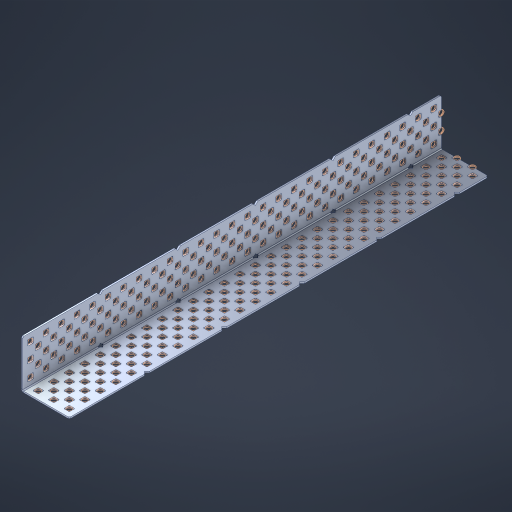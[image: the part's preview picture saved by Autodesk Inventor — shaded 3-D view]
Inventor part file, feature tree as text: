
AUTODESK INVENTOR PART (.ipt)
format: ipt  version: 2023 (Build 270158000, 158)  size: 2,800,128 bytes
history: native  units: in
note: dims shown in document units (in); Inventor stores cm internally (conversion verified against a paired STEP export)
features: extrude x62
bodies: Body1 (feature_tree), Body2 (feature_tree), Body3 (feature_tree), Body4 (feature_tree), Body5 (feature_tree), Body6 (feature_tree), Body7 (feature_tree), Body8 (feature_tree), Body9 (feature_tree), Body10 (feature_tree), Body11 (feature_tree), Body12 (feature_tree), Body13 (feature_tree), Body14 (feature_tree), Body15 (feature_tree), Body16 (feature_tree), Body17 (feature_tree), Body18 (feature_tree), Body19 (feature_tree), Body20 (feature_tree), Body21 (feature_tree), Body22 (feature_tree), Body23 (feature_tree), Body24 (feature_tree), Body25 (feature_tree), Body26 (feature_tree), Body27 (feature_tree), Body28 (feature_tree), Body29 (feature_tree), Body30 (feature_tree), Body31 (feature_tree), Body32 (feature_tree), Body33 (feature_tree), Body34 (feature_tree), Body35 (feature_tree), Body36 (feature_tree), Body37 (feature_tree), Body38 (feature_tree), Body39 (feature_tree), Body40 (feature_tree), Body41 (feature_tree), Body42 (feature_tree), Body43 (feature_tree), Body44 (feature_tree), Body45 (feature_tree), Body46 (feature_tree), Body47 (feature_tree), Body48 (feature_tree), Body49 (feature_tree), Body50 (feature_tree), Body51 (feature_tree), Body52 (feature_tree), Body53 (feature_tree), Body54 (feature_tree), Body55 (feature_tree), Body56 (feature_tree), Body57 (feature_tree), Body58 (feature_tree), Body59 (feature_tree), Body60 (feature_tree), Body61 (feature_tree), Body62 (feature_tree), Body63 (feature_tree), Body64 (feature_tree), Body65 (feature_tree), Body66 (feature_tree), Body67 (feature_tree), Body68 (feature_tree), Body69 (feature_tree), Body70 (feature_tree), Body71 (feature_tree), Body72 (feature_tree), Body73 (feature_tree), Body74 (feature_tree), Body75 (feature_tree), Body76 (feature_tree), Body77 (feature_tree), Body78 (feature_tree), Body79 (feature_tree), Body80 (feature_tree), Body81 (feature_tree), Body82 (feature_tree), Body83 (feature_tree), Body84 (feature_tree), Body85 (feature_tree), Body86 (feature_tree), Body87 (feature_tree), Body88 (feature_tree), Body89 (feature_tree), Body90 (feature_tree), Body91 (feature_tree), Body92 (feature_tree), Body93 (feature_tree), Body94 (feature_tree), Body95 (feature_tree), Body96 (feature_tree), Body97 (feature_tree), Body98 (feature_tree), Body99 (feature_tree), Body100 (feature_tree), Body101 (feature_tree), Body102 (feature_tree), Body103 (feature_tree), Body104 (feature_tree), Body105 (feature_tree), Body106 (feature_tree), Body107 (feature_tree), Body108 (feature_tree), Body109 (feature_tree), Body110 (feature_tree), Body111 (feature_tree), Body112 (feature_tree), Body113 (feature_tree), Body114 (feature_tree), Body115 (feature_tree), Body116 (feature_tree), Body117 (feature_tree), Body118 (feature_tree), Body119 (feature_tree), Body120 (feature_tree), Body121 (feature_tree), Body122 (feature_tree), Body123 (feature_tree), Body124 (feature_tree), Body125 (feature_tree), Body126 (feature_tree), Body127 (feature_tree), Body128 (feature_tree), Body129 (feature_tree), Body130 (feature_tree), Body131 (feature_tree), Body132 (feature_tree), Body133 (feature_tree), Body134 (feature_tree), Body135 (feature_tree), Body136 (feature_tree), Body137 (feature_tree), Body138 (feature_tree), Body139 (feature_tree), Body140 (feature_tree), Body141 (feature_tree), Body142 (feature_tree), Body143 (feature_tree), Body144 (feature_tree), Body145 (feature_tree), Body146 (feature_tree), Body147 (feature_tree), Body148 (feature_tree), Body149 (feature_tree), Body150 (feature_tree), Body151 (feature_tree), Body152 (feature_tree), Body153 (feature_tree), Body154 (feature_tree), Body155 (feature_tree), Body156 (feature_tree), Body157 (feature_tree), Body158 (feature_tree), Body159 (feature_tree), Body160 (feature_tree), Body161 (feature_tree), Body162 (feature_tree), Body163 (feature_tree), Body164 (feature_tree), Body165 (feature_tree), Body166 (feature_tree), Body167 (feature_tree), Body168 (feature_tree), Body169 (feature_tree), Body170 (feature_tree), Body171 (feature_tree), Body172 (feature_tree), Body173 (feature_tree), Body174 (feature_tree), Body175 (feature_tree), Body176 (feature_tree), Body177 (feature_tree), Body178 (feature_tree), Body179 (feature_tree), Body180 (feature_tree), Body181 (feature_tree), Body182 (feature_tree), Body183 (feature_tree), Body184 (feature_tree), Body185 (feature_tree), Body186 (feature_tree), Body187 (feature_tree), Body188 (feature_tree), Body189 (feature_tree), Body190 (feature_tree), Body191 (feature_tree), Body192 (feature_tree), Body193 (feature_tree), Body194 (feature_tree), Body195 (feature_tree), Body196 (feature_tree), Body197 (feature_tree), Body198 (feature_tree), Body199 (feature_tree), Body200 (feature_tree), Body201 (feature_tree), Body202 (feature_tree), Body203 (feature_tree), Body204 (feature_tree), Body205 (feature_tree), Body206 (feature_tree), Body207 (feature_tree), Body208 (feature_tree), Body209 (feature_tree), Body210 (feature_tree), Body211 (feature_tree), Body212 (feature_tree), Body213 (feature_tree), Body214 (feature_tree), Body215 (feature_tree), Body216 (feature_tree), Body217 (feature_tree), Body218 (feature_tree), Body219 (feature_tree), Body220 (feature_tree), Body221 (feature_tree), Body222 (feature_tree), Body223 (feature_tree), Body224 (feature_tree), Body225 (feature_tree), Body226 (feature_tree), Body227 (feature_tree), Body228 (feature_tree), Body229 (feature_tree), Body230 (feature_tree), Body231 (feature_tree), Body232 (feature_tree), Body233 (feature_tree), Body234 (feature_tree), Body235 (feature_tree), Body236 (feature_tree), Body237 (feature_tree), Body238 (feature_tree), Body239 (feature_tree), Body240 (feature_tree), Body241 (feature_tree), Body242 (feature_tree), Body243 (feature_tree), Body244 (feature_tree), Body245 (feature_tree), Body246 (feature_tree), Body247 (feature_tree), Body248 (feature_tree), Body249 (feature_tree), Body250 (feature_tree), Body251 (feature_tree), Body252 (feature_tree), Body253 (feature_tree), Body254 (feature_tree), Body255 (feature_tree), Body256 (feature_tree), Body257 (feature_tree), Body258 (feature_tree), Body259 (feature_tree), Body260 (feature_tree), Body261 (feature_tree), Body262 (feature_tree), Body263 (feature_tree), Body264 (feature_tree), Body265 (feature_tree), Body266 (feature_tree), Body267 (feature_tree), Body268 (feature_tree), Body269 (feature_tree), Body270 (feature_tree), Body271 (feature_tree)
feature tree (62):
  extrude  "ExtrusionSrf2195"  Depth=1.5in
  extrude  "ExtrusionSrf2196"  Depth=13.5in
  extrude  "ExtrusionSrf2197"  Depth=0.0469in
  extrude  "ExtrusionSrf2198"  Depth=0.0469in
  extrude  "ExtrusionSrf2199"  Depth=0.0234in
  extrude  "ExtrusionSrf2200"  Depth=0.0938in
  extrude  "ExtrusionSrf2201"  Depth=0.0469in
  extrude  "ExtrusionSrf2202"  Depth=1.5in TaperAngle=90.0deg
  extrude  "ExtrusionSrf2203"  Depth=0.1875in
  extrude  "ExtrusionSrf2204"  Depth=0.0469in
  extrude  "ExtrusionSrf2205"  Depth=0.0469in
  extrude  "ExtrusionSrf2206"  Depth=0.182in
  extrude  "ExtrusionSrf2207"  Depth=0.02in
  extrude  "ExtrusionSrf2208"  Depth=0.25in
  extrude  "ExtrusionSrf2209"  Depth=0.0469in
  extrude  "ExtrusionSrf2210"  TaperAngle=0.0deg  [1 undecoded]
  extrude  "ExtrusionSrf2211"  Depth=0.172in
  extrude  "ExtrusionSrf2212"  Depth=1.0in TaperAngle=0.0deg
  extrude  "ExtrusionSrf2213"  Depth=0.1473in
  extrude  "ExtrusionSrf2214"  Depth=0.1659in
  extrude  "ExtrusionSrf2215"  Depth=0.0469in
  extrude  "ExtrusionSrf2216"  Depth=0.04in TaperAngle=0.0deg
  extrude  "ExtrusionSrf2217"  Depth=2.5in
  extrude  "ExtrusionSrf2218"  Depth=0.25in TaperAngle=45.0deg
  extrude  "ExtrusionSrf2219"  Depth=0.182in
  extrude  "ExtrusionSrf2220"  Depth=0.02in
  extrude  "ExtrusionSrf2221"  Depth=0.0469in
  extrude  "ExtrusionSrf2222"  TaperAngle=0.0deg  [1 undecoded]
  extrude  "ExtrusionSrf2223"  Depth=0.172in
  extrude  "ExtrusionSrf2224"  Depth=0.5in TaperAngle=0.0deg
  extrude  "ExtrusionSrf2225"  Depth=0.5in
  extrude  "ExtrusionSrf2226"  Depth=0.0491in
  extrude  "ExtrusionSrf2227"  Depth=0.1227in
  extrude  "ExtrusionSrf2228"  Depth=0.08in
  extrude  "ExtrusionSrf2229"  Depth=0.04in
  extrude  "ExtrusionSrf2230"  Depth=2.5in
  extrude  "ExtrusionSrf2231"  Depth=0.25in
  extrude  "ExtrusionSrf2232"  Depth=10.6299in
  extrude  "ExtrusionSrf2233"  Depth=0.5in
  extrude  "ExtrusionSrf2234"  Depth=0.5in
  extrude  "ExtrusionSrf2235"  Depth=1.0in
  extrude  "ExtrusionSrf2236"  Depth=0.3937in
  extrude  "ExtrusionSrf2237"  Depth=0.071in
  extrude  "ExtrusionSrf2238"  Depth=0.5in
  extrude  "ExtrusionSrf2239"  [1 undecoded]
  extrude  "ExtrusionSrf2240"  [1 undecoded]
  extrude  "ExtrusionSrf2241"  [1 undecoded]
  extrude  "ExtrusionSrf2242"  [1 undecoded]
  extrude  "ExtrusionSrf2243"  [1 undecoded]
  extrude  "ExtrusionSrf2244"  [1 undecoded]
  extrude  "ExtrusionSrf2245"  [1 undecoded]
  extrude  "ExtrusionSrf2246"  [1 undecoded]
  extrude  "ExtrusionSrf2247"  [1 undecoded]
  extrude  "ExtrusionSrf2248"  [1 undecoded]
  extrude  "ExtrusionSrf2249"  [1 undecoded]
  extrude  "ExtrusionSrf2250"  [1 undecoded]
  extrude  "ExtrusionSrf2251"  [1 undecoded]
  extrude  "ExtrusionSrf2252"  [1 undecoded]
  extrude  "ExtrusionSrf2253"  [1 undecoded]
  extrude  "ExtrusionSrf2254"  [1 undecoded]
  extrude  "ExtrusionSrf2255"  [1 undecoded]
  extrude  "ExtrusionSrf2256"  [1 undecoded]
note: 20 required parameter values undecoded (feature->parameter linkage not recoverable at this tier; creation-order binding heuristic only, values carry confidence <= 0.55)
